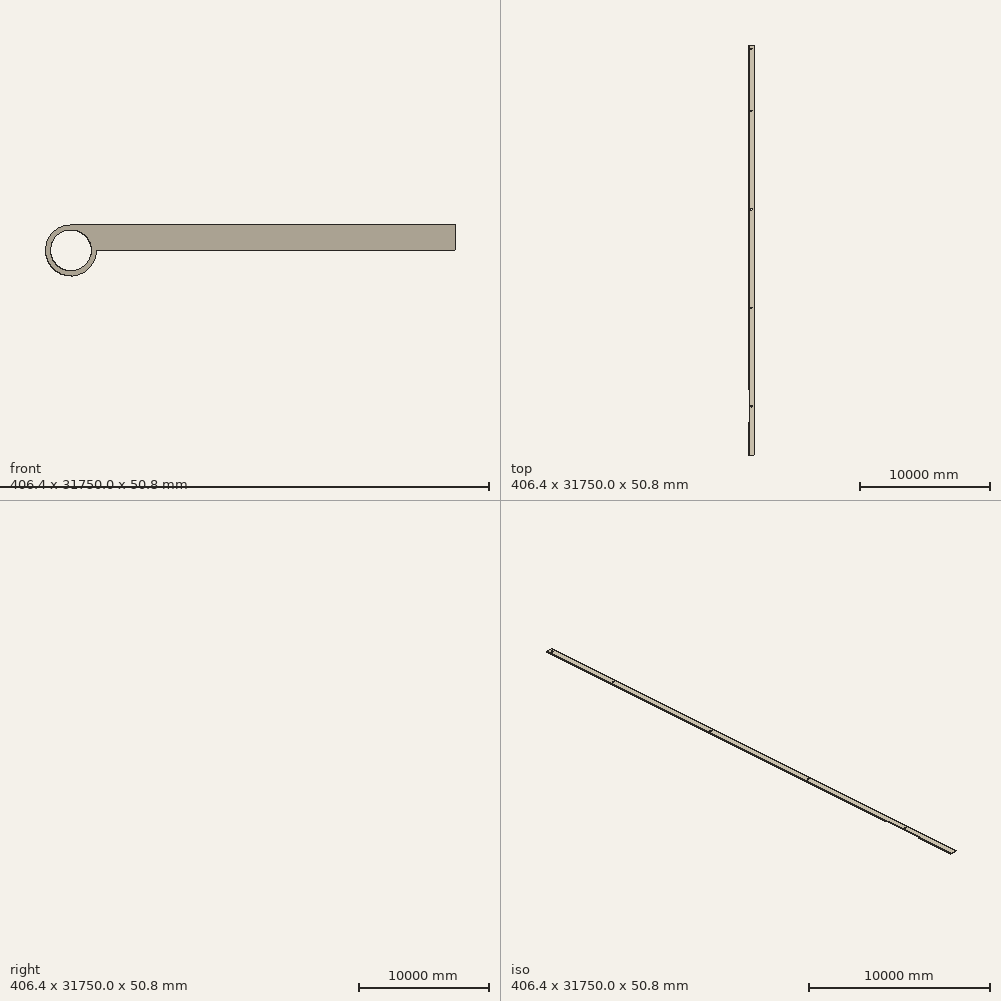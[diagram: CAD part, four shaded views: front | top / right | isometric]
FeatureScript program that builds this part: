
annotation { "Feature Type Name" : "Feature", "Feature Type Description" : "" }
export const myFeature = defineFeature(function(context is Context, id is Id, definition is map)
    precondition{}
    {
        {
            var Q0;
            Q0=qCreatedBy(makeId("Top.planeOp"),FACE);
            var sketch = newSketch(context, id + "F0", { "sketchPlane" : qUnion([Q0])});
            skLineSegment(sketch, "E0.bottom", {"start": v(-137.34, 31736.46) * mm, "end": v(243.66, 31736.46) * mm});
            skLineSegment(sketch, "E0.top", {"start": v(-137.34, -13.54) * mm, "end": v(243.66, -13.54) * mm});
            skLineSegment(sketch, "E0.left", {"start": v(-137.34, 31736.46) * mm, "end": v(-137.34, -13.54) * mm});
            skLineSegment(sketch, "E0.right", {"start": v(243.66, 31736.46) * mm, "end": v(243.66, -13.54) * mm});
            skSolve(sketch);
        }
        {
            var Q0;
            Q0 = qSketchRegion(id + "F0", true);
            extrude(context, id + "F1", {"entities" : qUnion([Q0]), "depth" : 25.4 * mm, "offsetDistance" : 25.4 * mm});
        }
        {
            var Q0;
            Q0=makeQuery(id+"F1.opExtrude","SWEPT_FACE",FACE,{"disambiguationData":[OSD([sQuery(id+"F0.wireOp",EDGE,"E0.bottom")])]});
            var sketch = newSketch(context, id + "F2", { "sketchPlane" : qUnion([Q0])});
            skCircle(sketch, "E1", {"center": v(137.34, 0) * mm, "radius": 25.4 * mm});
            skSolve(sketch);
        }
        {
            var Q0;
            {var subQ1=sQuery(id+"F0.wireOp",EDGE,"E0.bottom");var subQ2=makeQuery(id+"F1.opExtrude","SWEPT_EDGE",EDGE,{"disambiguationData":[OSD([subQ1,sQuery(id+"F0.wireOp",EDGE,"E0.left")])]});Q0=makeQuery(id+"F2.imprint","IMPRINT",FACE,{"disambiguationData":[TD([[makeQuery(id+"F2.imprint","IMPRINT",EDGE,{"derivedFrom":subQ2}),1.0]])]});}
            var Q1;
            Q1=makeQuery(id+"F1.opExtrude","CAP_EDGE",EDGE,{"disambiguationData":[OSD([sQuery(id+"F0.wireOp",EDGE,"E0.left")])],"isStart":true});
            sweep(context, id + "F3", {"operationType" : NewBodyOperationType.ADD, "profiles" : qUnion([Q0]), "path" : qUnion([Q1])});
        }
        {
            var Q0;
            {var subQ0=sQuery(id+"F0.wireOp",EDGE,"E0.bottom");Q0=makeQuery(id+"F3.boolean.opBoolean","MERGE",FACE,{"derivedFrom":[makeQuery(id+"F1.opExtrude","SWEPT_FACE",FACE,{"disambiguationData":[OSD([subQ0])]}),makeQuery(id+"F3.opSweep","CAP_FACE",FACE,{"disambiguationData":[OSD([subQ0,sQuery(id+"F0.wireOp",EDGE,"E0.left"),sQuery(id+"F2.wireOp",EDGE,"E1")])],"isStart":true})]});}
            var sketch = newSketch(context, id + "F4", { "sketchPlane" : qUnion([Q0])});
            skCircle(sketch, "E2", {"center": v(137.34, 0) * mm, "radius": 20.32 * mm});
            skSolve(sketch);
        }
        {
            var Q0;
            Q0 = qSketchRegion(id + "F4", true);
            extrude(context, id + "F5", {"entities" : qUnion([Q0]), "operationType" : NewBodyOperationType.REMOVE, "endBound" : BoundingType.THROUGH_ALL, "oppositeDirection" : true, "depth" : 25.4 * mm, "offsetDistance" : 25.4 * mm});
        }
        {
            var Q0;
            Q0=makeQuery(id+"F1.opExtrude","CAP_FACE",FACE,{"disambiguationData":[OSD([sQuery(id+"F0.wireOp",EDGE,"E0.bottom"),sQuery(id+"F0.wireOp",EDGE,"E0.top"),sQuery(id+"F0.wireOp",EDGE,"E0.left"),sQuery(id+"F0.wireOp",EDGE,"E0.right")])],"isStart":true});
            var sketch = newSketch(context, id + "F6", { "sketchPlane" : qUnion([Q0])});
            skLineSegment(sketch, "E3", {"start": v(-111.94, 13.54) * mm, "end": v(-111.94, -2526.46) * mm, "construction": true});
            skLineSegment(sketch, "E4.bottom", {"start": v(-111.94, -2526.46) * mm, "end": v(-442.32, -2526.46) * mm});
            skLineSegment(sketch, "E4.top", {"start": v(-111.94, -5066.46) * mm, "end": v(-442.32, -5066.46) * mm});
            skLineSegment(sketch, "E4.left", {"start": v(-111.94, -2526.46) * mm, "end": v(-111.94, -5066.46) * mm});
            skLineSegment(sketch, "E4.right", {"start": v(-442.32, -2526.46) * mm, "end": v(-442.32, -5066.46) * mm});
            skLineSegment(sketch, "E5.0.1.0", {"start": v(-111.94, -2526.46) * mm, "end": v(-111.94, -5066.46) * mm, "construction": true});
            skLineSegment(sketch, "E5.0.1.2", {"start": v(-442.32, -5066.46) * mm, "end": v(-442.32, -7606.46) * mm});
            skLineSegment(sketch, "E5.0.1.3", {"start": v(-111.94, -5066.46) * mm, "end": v(-111.94, -7606.46) * mm});
            skLineSegment(sketch, "E5.0.1.4", {"start": v(-111.94, -7606.46) * mm, "end": v(-442.32, -7606.46) * mm});
            skLineSegment(sketch, "E5.0.2.0", {"start": v(-111.94, -5066.46) * mm, "end": v(-111.94, -7606.46) * mm, "construction": true});
            skLineSegment(sketch, "E5.0.2.1", {"start": v(-111.94, -7606.46) * mm, "end": v(-442.32, -7606.46) * mm});
            skLineSegment(sketch, "E5.0.2.2", {"start": v(-442.32, -7606.46) * mm, "end": v(-442.32, -10146.46) * mm});
            skLineSegment(sketch, "E5.0.2.3", {"start": v(-111.94, -7606.46) * mm, "end": v(-111.94, -10146.46) * mm});
            skLineSegment(sketch, "E5.0.2.4", {"start": v(-111.94, -10146.46) * mm, "end": v(-442.32, -10146.46) * mm});
            skLineSegment(sketch, "E5.0.3.0", {"start": v(-111.94, -7606.46) * mm, "end": v(-111.94, -10146.46) * mm, "construction": true});
            skLineSegment(sketch, "E5.0.3.1", {"start": v(-111.94, -10146.46) * mm, "end": v(-442.32, -10146.46) * mm});
            skLineSegment(sketch, "E5.0.3.2", {"start": v(-442.32, -10146.46) * mm, "end": v(-442.32, -12686.46) * mm});
            skLineSegment(sketch, "E5.0.3.3", {"start": v(-111.94, -10146.46) * mm, "end": v(-111.94, -12686.46) * mm});
            skLineSegment(sketch, "E5.0.3.4", {"start": v(-111.94, -12686.46) * mm, "end": v(-442.32, -12686.46) * mm});
            skLineSegment(sketch, "E5.0.4.0", {"start": v(-111.94, -10146.46) * mm, "end": v(-111.94, -12686.46) * mm, "construction": true});
            skLineSegment(sketch, "E5.0.4.1", {"start": v(-111.94, -12686.46) * mm, "end": v(-442.32, -12686.46) * mm});
            skLineSegment(sketch, "E5.0.4.2", {"start": v(-442.32, -12686.46) * mm, "end": v(-442.32, -15226.46) * mm});
            skLineSegment(sketch, "E5.0.4.3", {"start": v(-111.94, -12686.46) * mm, "end": v(-111.94, -15226.46) * mm});
            skLineSegment(sketch, "E5.0.4.4", {"start": v(-111.94, -15226.46) * mm, "end": v(-442.32, -15226.46) * mm});
            skLineSegment(sketch, "E5.0.5.0", {"start": v(-111.94, -12686.46) * mm, "end": v(-111.94, -15226.46) * mm, "construction": true});
            skLineSegment(sketch, "E5.0.5.1", {"start": v(-111.94, -15226.46) * mm, "end": v(-442.32, -15226.46) * mm});
            skLineSegment(sketch, "E5.0.5.2", {"start": v(-442.32, -15226.46) * mm, "end": v(-442.32, -17766.46) * mm});
            skLineSegment(sketch, "E5.0.5.3", {"start": v(-111.94, -15226.46) * mm, "end": v(-111.94, -17766.46) * mm});
            skLineSegment(sketch, "E5.0.5.4", {"start": v(-111.94, -17766.46) * mm, "end": v(-442.32, -17766.46) * mm});
            skLineSegment(sketch, "E5.0.6.0", {"start": v(-111.94, -15226.46) * mm, "end": v(-111.94, -17766.46) * mm, "construction": true});
            skLineSegment(sketch, "E5.0.6.1", {"start": v(-111.94, -17766.46) * mm, "end": v(-442.32, -17766.46) * mm});
            skLineSegment(sketch, "E5.0.6.2", {"start": v(-442.32, -17766.46) * mm, "end": v(-442.32, -20306.46) * mm});
            skLineSegment(sketch, "E5.0.6.3", {"start": v(-111.94, -17766.46) * mm, "end": v(-111.94, -20306.46) * mm});
            skLineSegment(sketch, "E5.0.6.4", {"start": v(-111.94, -20306.46) * mm, "end": v(-442.32, -20306.46) * mm});
            skLineSegment(sketch, "E5.0.7.0", {"start": v(-111.94, -17766.46) * mm, "end": v(-111.94, -20306.46) * mm, "construction": true});
            skLineSegment(sketch, "E5.0.7.1", {"start": v(-111.94, -20306.46) * mm, "end": v(-442.32, -20306.46) * mm});
            skLineSegment(sketch, "E5.0.7.2", {"start": v(-442.32, -20306.46) * mm, "end": v(-442.32, -22846.46) * mm});
            skLineSegment(sketch, "E5.0.7.3", {"start": v(-111.94, -20306.46) * mm, "end": v(-111.94, -22846.46) * mm});
            skLineSegment(sketch, "E5.0.7.4", {"start": v(-111.94, -22846.46) * mm, "end": v(-442.32, -22846.46) * mm});
            skLineSegment(sketch, "E5.0.8.0", {"start": v(-111.94, -20306.46) * mm, "end": v(-111.94, -22846.46) * mm, "construction": true});
            skLineSegment(sketch, "E5.0.8.1", {"start": v(-111.94, -22846.46) * mm, "end": v(-442.32, -22846.46) * mm});
            skLineSegment(sketch, "E5.0.8.2", {"start": v(-442.32, -22846.46) * mm, "end": v(-442.32, -25386.46) * mm});
            skLineSegment(sketch, "E5.0.8.3", {"start": v(-111.94, -22846.46) * mm, "end": v(-111.94, -25386.46) * mm});
            skLineSegment(sketch, "E5.0.8.4", {"start": v(-111.94, -25386.46) * mm, "end": v(-442.32, -25386.46) * mm});
            skLineSegment(sketch, "E5.0.9.0", {"start": v(-111.94, -22846.46) * mm, "end": v(-111.94, -25386.46) * mm, "construction": true});
            skLineSegment(sketch, "E5.0.9.1", {"start": v(-111.94, -25386.46) * mm, "end": v(-442.32, -25386.46) * mm});
            skLineSegment(sketch, "E5.0.9.2", {"start": v(-442.32, -25386.46) * mm, "end": v(-442.32, -27926.46) * mm});
            skLineSegment(sketch, "E5.0.9.3", {"start": v(-111.94, -25386.46) * mm, "end": v(-111.94, -27926.46) * mm});
            skLineSegment(sketch, "E5.0.9.4", {"start": v(-111.94, -27926.46) * mm, "end": v(-442.32, -27926.46) * mm});
            skLineSegment(sketch, "E5.0.10.0", {"start": v(-111.94, -25386.46) * mm, "end": v(-111.94, -27926.46) * mm, "construction": true});
            skLineSegment(sketch, "E5.0.10.1", {"start": v(-111.94, -27926.46) * mm, "end": v(-442.32, -27926.46) * mm});
            skLineSegment(sketch, "E5.0.10.2", {"start": v(-442.32, -27926.46) * mm, "end": v(-442.32, -30466.46) * mm});
            skLineSegment(sketch, "E5.0.10.3", {"start": v(-111.94, -27926.46) * mm, "end": v(-111.94, -30466.46) * mm});
            skLineSegment(sketch, "E5.0.10.4", {"start": v(-111.94, -30466.46) * mm, "end": v(-442.32, -30466.46) * mm});
            skLineSegment(sketch, "E5.direction1", {"start": v(-111.94, -2526.46) * mm, "end": v(-86.54, -2526.46) * mm, "construction": true});
            skLineSegment(sketch, "E5.direction2", {"start": v(-111.94, -2526.46) * mm, "end": v(-111.94, -5066.46) * mm, "construction": true});
            skSolve(sketch);
        }
        {
            var Q0;
            Q0=makeQuery(id+"F6.imprint","IMPRINT",FACE,{"disambiguationData":[TD([[makeQuery(id+"F6.imprint","IMPRINT",EDGE,{"derivedFrom":sQuery(id+"F6.wireOp",EDGE,"E4.bottom")}),1.0]])]});
            var Q1;
            Q1=makeQuery(id+"F6.imprint","IMPRINT",FACE,{"disambiguationData":[TD([[makeQuery(id+"F6.imprint","IMPRINT",EDGE,{"derivedFrom":sQuery(id+"F6.wireOp",EDGE,"E5.0.2.1")}),1.0]])]});
            var Q2;
            Q2=makeQuery(id+"F6.imprint","IMPRINT",FACE,{"disambiguationData":[TD([[makeQuery(id+"F6.imprint","IMPRINT",EDGE,{"derivedFrom":sQuery(id+"F6.wireOp",EDGE,"E5.0.4.1")}),1.0]])]});
            var Q3;
            Q3=makeQuery(id+"F6.imprint","IMPRINT",FACE,{"disambiguationData":[TD([[makeQuery(id+"F6.imprint","IMPRINT",EDGE,{"derivedFrom":sQuery(id+"F6.wireOp",EDGE,"E5.0.6.1")}),1.0]])]});
            var Q4;
            Q4=makeQuery(id+"F6.imprint","IMPRINT",FACE,{"disambiguationData":[TD([[makeQuery(id+"F6.imprint","IMPRINT",EDGE,{"derivedFrom":sQuery(id+"F6.wireOp",EDGE,"E5.0.8.1")}),1.0]])]});
            var Q5;
            Q5=makeQuery(id+"F6.imprint","IMPRINT",FACE,{"disambiguationData":[TD([[makeQuery(id+"F6.imprint","IMPRINT",EDGE,{"derivedFrom":sQuery(id+"F6.wireOp",EDGE,"E5.0.10.1")}),1.0]])]});
            extrude(context, id + "F7", {"entities" : qUnion([Q0, Q1, Q2, Q3, Q4, Q5]), "operationType" : NewBodyOperationType.REMOVE, "endBound" : BoundingType.SYMMETRIC, "oppositeDirection" : true, "depth" : 254 * mm, "offsetDistance" : 25.4 * mm});
        }
        {
            var Q0;
            Q0=makeQuery(id+"F1.opExtrude","CAP_FACE",FACE,{"disambiguationData":[OSD([sQuery(id+"F0.wireOp",EDGE,"E0.bottom"),sQuery(id+"F0.wireOp",EDGE,"E0.top"),sQuery(id+"F0.wireOp",EDGE,"E0.left"),sQuery(id+"F0.wireOp",EDGE,"E0.right")])],"isStart":true});
            var sketch = newSketch(context, id + "F8", { "sketchPlane" : qUnion([Q0])});
            skLineSegment(sketch, "E6", {"start": v(48.14, -31736.46) * mm, "end": v(48.14, 1283.54) * mm, "construction": true});
            skPoint(sketch, "E7", {"position": v(48.14, -31482.46) * mm});
            skPoint(sketch, "E8", {"position": v(48.14, -26656.46) * mm});
            skPoint(sketch, "E9", {"position": v(48.14, -19036.46) * mm});
            skPoint(sketch, "E10", {"position": v(48.14, -11416.46) * mm});
            skPoint(sketch, "E11", {"position": v(48.14, -3796.46) * mm});
            skPoint(sketch, "E12", {"position": v(48.14, 1029.54) * mm});
            skSolve(sketch);
        }
        {
            var Q0;
            Q0=sQuery(id+"F8.wireOp",VERTEX,"E12");
            var Q1;
            Q1=sQuery(id+"F8.wireOp",VERTEX,"E11");
            var Q2;
            Q2=sQuery(id+"F8.wireOp",VERTEX,"E10");
            var Q3;
            Q3=sQuery(id+"F8.wireOp",VERTEX,"E8");
            var Q4;
            Q4=sQuery(id+"F8.wireOp",VERTEX,"E9");
            var Q5;
            Q5=sQuery(id+"F8.wireOp",VERTEX,"E7");
            var Q6;
            Q6=makeQuery(id+"F1.opExtrude","SWEPT_BODY",BODY,{"disambiguationData":[OSD([sQuery(id+"F0.wireOp",EDGE,"E0.bottom"),sQuery(id+"F0.wireOp",EDGE,"E0.top"),sQuery(id+"F0.wireOp",EDGE,"E0.left"),sQuery(id+"F0.wireOp",EDGE,"E0.right")])]});
            hole(context, id + "F9", {"style" : HoleStyle.C_SINK, "endStyle" : HoleEndStyle.THROUGH, "holeDiameter" : 101.6 * mm, "cSinkDiameter" : 203.2 * mm, "cSinkAngle" : 110 * degree, "majorDiameter" : 6.35 * mm, "isTappedThrough" : true, "tappedDepth" : 12.7 * mm, "tapClearance" : 3, "locations" : qUnion([Q0, Q1, Q2, Q3, Q4, Q5]), "scope" : qUnion([Q6])});
        }
    });
